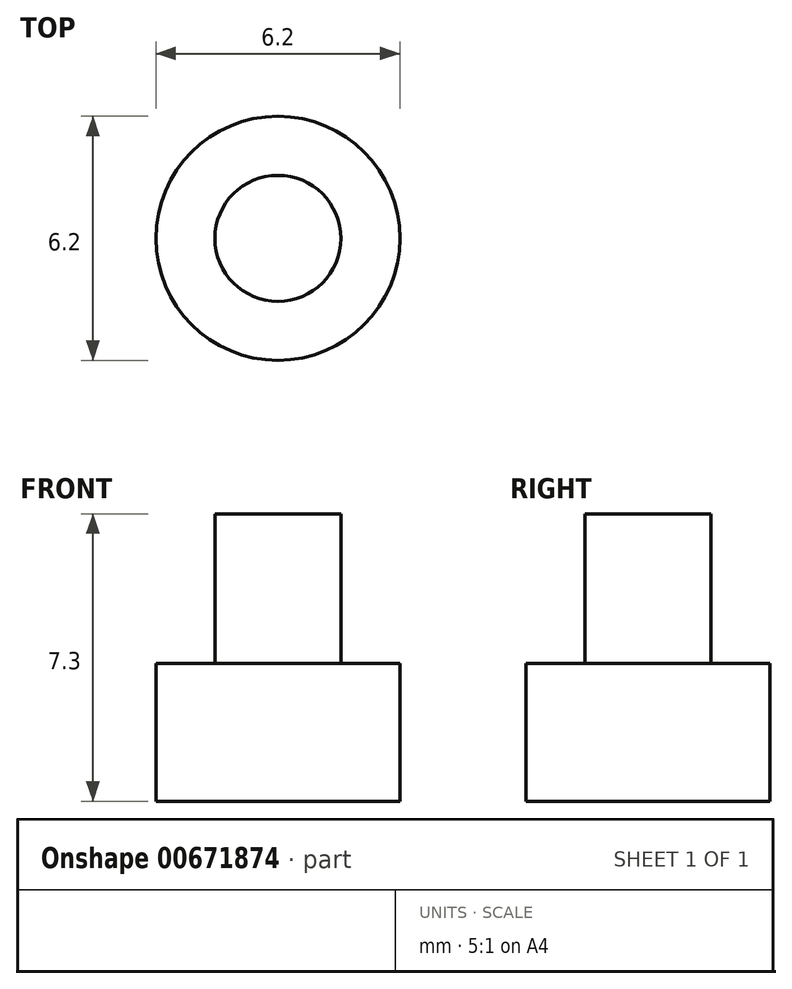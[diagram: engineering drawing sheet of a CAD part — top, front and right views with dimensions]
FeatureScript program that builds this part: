
annotation { "Feature Type Name" : "Feature", "Feature Type Description" : "" }
export const myFeature = defineFeature(function(context is Context, id is Id, definition is map)
    precondition{}
    {
        {
            var Q0;
            Q0=qCreatedBy(makeId("Front.planeOp"),FACE);
            var sketch = newSketch(context, id + "F0", { "sketchPlane" : qUnion([Q0])});
            skLineSegment(sketch, "E0", {"start": v(0, 0) * mm, "end": v(3.1, 0) * mm});
            skLineSegment(sketch, "E1", {"start": v(3.1, 0) * mm, "end": v(3.1, 3.5) * mm});
            skLineSegment(sketch, "E2", {"start": v(3.1, 3.5) * mm, "end": v(1.6, 3.5) * mm});
            skLineSegment(sketch, "E3", {"start": v(1.6, 3.5) * mm, "end": v(1.6, 7.3) * mm});
            skLineSegment(sketch, "E4", {"start": v(1.6, 7.3) * mm, "end": v(0, 7.3) * mm});
            skLineSegment(sketch, "E5", {"start": v(0, 7.3) * mm, "end": v(0, 0) * mm});
            skSolve(sketch);
        }
        {
            var Q0;
            Q0=makeQuery(id+"F0.imprint","IMPRINT",FACE,{"disambiguationData":[TD([[makeQuery(id+"F0.imprint","IMPRINT",EDGE,{"derivedFrom":sQuery(id+"F0.wireOp",EDGE,"E0")}),1.0]])]});
            var Q1;
            Q1=sQuery(id+"F0.wireOp",EDGE,"E5");
            revolve(context, id + "F1", {"surfaceOperationType" : NewSurfaceOperationType.NEW, "entities" : qUnion([Q0]), "axis" : qUnion([Q1]), "revolveType" : RevolveType.FULL});
        }
    });
